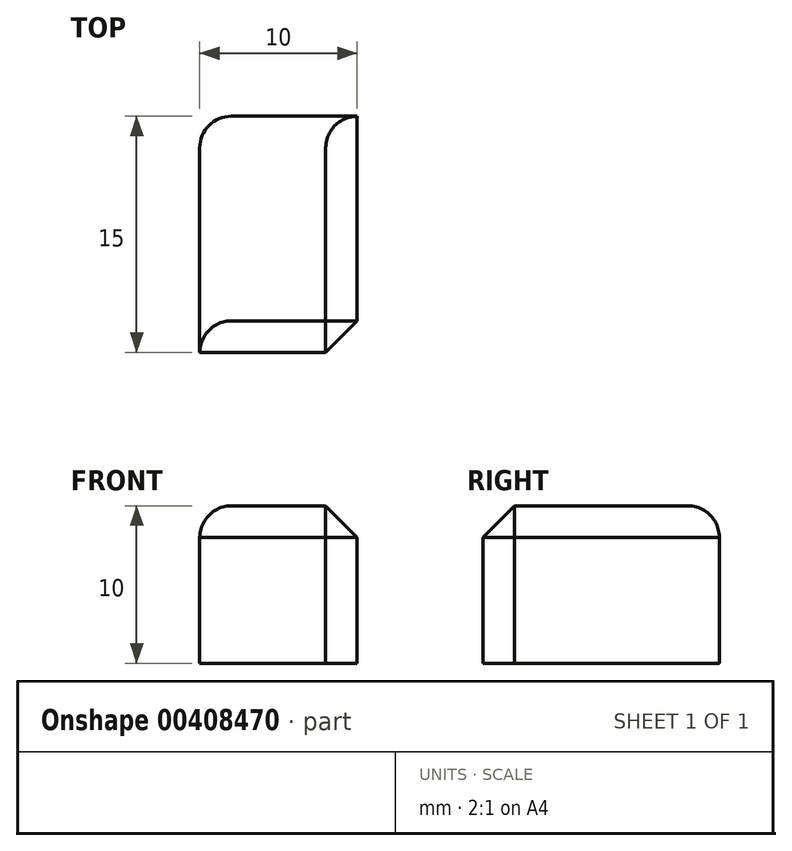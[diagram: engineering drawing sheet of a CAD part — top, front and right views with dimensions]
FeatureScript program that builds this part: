
annotation { "Feature Type Name" : "Feature", "Feature Type Description" : "" }
export const myFeature = defineFeature(function(context is Context, id is Id, definition is map)
    precondition{}
    {
        {
            var Q0;
            Q0=qCreatedBy(makeId("Front.planeOp"),FACE);
            var sketch = newSketch(context, id + "F0", { "sketchPlane" : qUnion([Q0])});
            skLineSegment(sketch, "E0.bottom", {"start": v(0, 0) * mm, "end": v(-10, 0) * mm});
            skLineSegment(sketch, "E0.top", {"start": v(0, 10) * mm, "end": v(-10, 10) * mm});
            skLineSegment(sketch, "E0.left", {"start": v(0, 0) * mm, "end": v(0, 10) * mm});
            skLineSegment(sketch, "E0.right", {"start": v(-10, 0) * mm, "end": v(-10, 10) * mm});
            skLineSegment(sketch, "E1", {"start": v(13.93, 0) * mm, "end": v(-37.55, 0) * mm, "construction": true});
            skLineSegment(sketch, "E2", {"start": v(0, 32.4) * mm, "end": v(0, -18.87) * mm, "construction": true});
            skSolve(sketch);
        }
        {
            var Q0;
            Q0 = qSketchRegion(id + "F0", true);
            extrude(context, id + "F1", {"entities" : qUnion([Q0]), "depth" : 15 * mm});
        }
        {
            var Q0;
            Q0=makeQuery(id+"F1.opExtrude","CAP_EDGE",EDGE,{"disambiguationData":[OSD([sQuery(id+"F0.wireOp",EDGE,"E0.top")])],"isStart":false});
            var Q1;
            Q1=makeQuery(id+"F1.opExtrude","CAP_EDGE",EDGE,{"disambiguationData":[OSD([sQuery(id+"F0.wireOp",EDGE,"E0.left")])],"isStart":false});
            var Q2;
            Q2=makeQuery(id+"F1.opExtrude","SWEPT_EDGE",EDGE,{"disambiguationData":[OSD([sQuery(id+"F0.wireOp",EDGE,"E0.top"),sQuery(id+"F0.wireOp",EDGE,"E0.left")])]});
            chamfer(context, id + "F2", {"entities" : qUnion([Q0, Q1, Q2]), "width" : 2 * mm, "tangentPropagation" : true});
        }
        {
            var Q0;
            Q0=makeQuery(id+"F1.opExtrude","CAP_EDGE",EDGE,{"disambiguationData":[OSD([sQuery(id+"F0.wireOp",EDGE,"E0.right")])],"isStart":true});
            var Q1;
            Q1=makeQuery(id+"F1.opExtrude","CAP_EDGE",EDGE,{"disambiguationData":[OSD([sQuery(id+"F0.wireOp",EDGE,"E0.top")])],"isStart":true});
            var Q2;
            Q2=makeQuery(id+"F1.opExtrude","SWEPT_EDGE",EDGE,{"disambiguationData":[OSD([sQuery(id+"F0.wireOp",EDGE,"E0.top"),sQuery(id+"F0.wireOp",EDGE,"E0.right")])]});
            fillet(context, id + "F3", {"entities" : qUnion([Q0, Q1, Q2]), "radius" : 2 * mm, "tangentPropagation" : true, "allowEdgeOverflow" : false});
        }
    });
